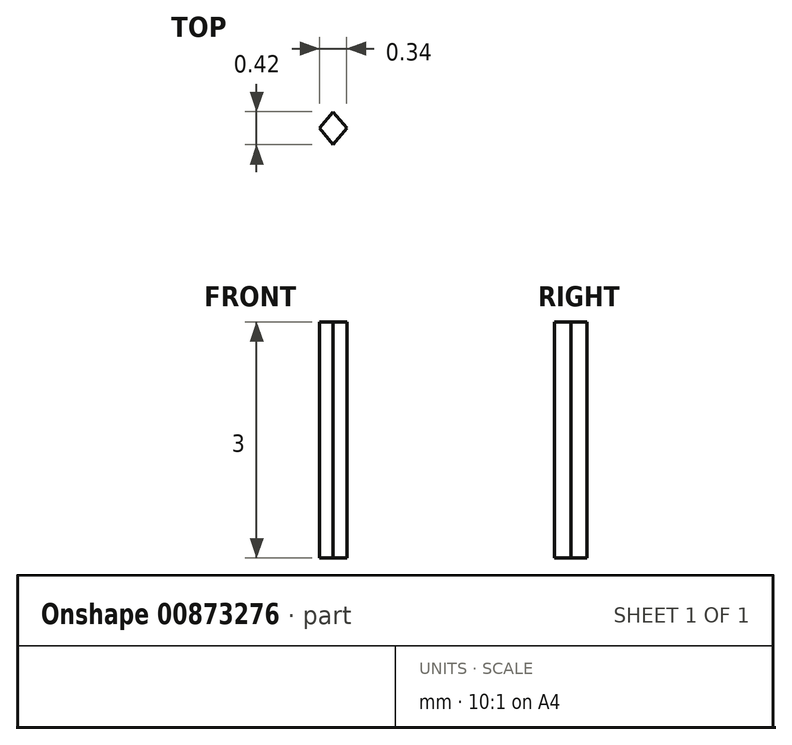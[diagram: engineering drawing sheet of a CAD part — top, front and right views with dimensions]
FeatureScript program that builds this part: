
annotation { "Feature Type Name" : "Feature", "Feature Type Description" : "" }
export const myFeature = defineFeature(function(context is Context, id is Id, definition is map)
    precondition{}
    {
        {
            var Q0;
            Q0=qCreatedBy(makeId("Top.planeOp"),FACE);
            var sketch = newSketch(context, id + "F0", { "sketchPlane" : qUnion([Q0])});
            skLineSegment(sketch, "E0", {"start": v(0, 45) * mm, "end": v(38, 0) * mm});
            skLineSegment(sketch, "E1", {"start": v(38, 0) * mm, "end": v(0, -45) * mm});
            skLineSegment(sketch, "E2", {"start": v(0, -45) * mm, "end": v(-38, 0) * mm});
            skLineSegment(sketch, "E3", {"start": v(-38, 0) * mm, "end": v(0, 45) * mm});
            skLineSegment(sketch, "E4.0", {"start": v(0.17, 0) * mm, "end": v(0, -0.2) * mm});
            skLineSegment(sketch, "E4.1", {"start": v(0, 0.2) * mm, "end": v(0.17, 0) * mm});
            skLineSegment(sketch, "E4.2", {"start": v(-0.17, 0) * mm, "end": v(0, 0.2) * mm});
            skLineSegment(sketch, "E4.3", {"start": v(0, -0.2) * mm, "end": v(-0.17, 0) * mm});
            skSolve(sketch);
        }
        {
            var Q0;
            Q0=makeQuery(id+"F0.imprint","IMPRINT",FACE,{"disambiguationData":[TD([[makeQuery(id+"F0.imprint","IMPRINT",EDGE,{"derivedFrom":sQuery(id+"F0.wireOp",EDGE,"E4.0")}),-1.0]])]});
            extrude(context, id + "F1", {"entities" : qUnion([Q0]), "depth" : 3 * mm, "offsetDistance" : 25 * mm});
        }
    });
